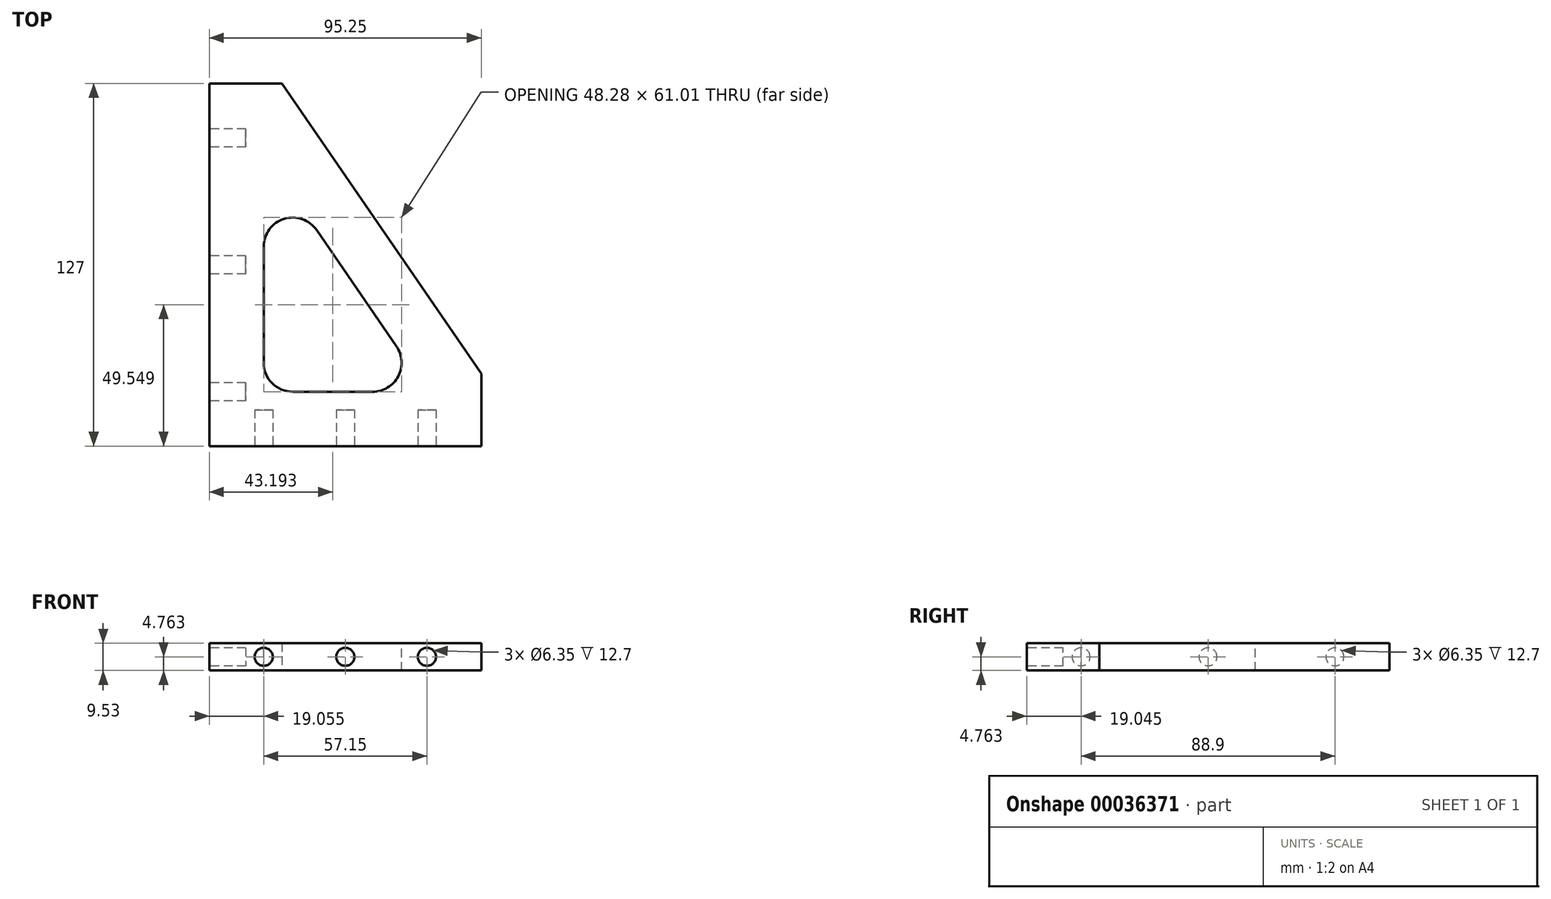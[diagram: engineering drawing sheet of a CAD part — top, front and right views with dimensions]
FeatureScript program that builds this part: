
annotation { "Feature Type Name" : "Feature", "Feature Type Description" : "" }
export const myFeature = defineFeature(function(context is Context, id is Id, definition is map)
    precondition{}
    {
        {
            var Q0;
            Q0=qCreatedBy(makeId("Top.planeOp"),FACE);
            var sketch = newSketch(context, id + "F0", { "sketchPlane" : qUnion([Q0])});
            skLineSegment(sketch, "E0", {"start": v(-41.93, 63.48) * mm, "end": v(-41.93, -63.52) * mm});
            skLineSegment(sketch, "E1", {"start": v(-41.93, 63.48) * mm, "end": v(-16.53, 63.48) * mm});
            skLineSegment(sketch, "E2", {"start": v(-41.93, -63.52) * mm, "end": v(53.32, -63.52) * mm});
            skLineSegment(sketch, "E3", {"start": v(53.32, -63.52) * mm, "end": v(53.32, -38.12) * mm});
            skLineSegment(sketch, "E4", {"start": v(-16.53, 63.48) * mm, "end": v(53.32, -38.12) * mm});
            skSolve(sketch);
        }
        {
            var Q0;
            Q0=makeQuery(id+"F0.imprint","IMPRINT",FACE,{"disambiguationData":[TD([[makeQuery(id+"F0.imprint","IMPRINT",EDGE,{"derivedFrom":sQuery(id+"F0.wireOp",EDGE,"E0")}),1.0]])]});
            var Q1;
            Q1 = qSketchRegion(id + "F0", true);
            extrude(context, id + "F1", {"entities" : qUnion([Q0, Q1]), "depth" : 9.52 * mm});
        }
        {
            var Q0;
            Q0=makeQuery(id+"F1.opExtrude","CAP_FACE",FACE,{"disambiguationData":[OSD([sQuery(id+"F0.wireOp",EDGE,"E0"),sQuery(id+"F0.wireOp",EDGE,"E1"),sQuery(id+"F0.wireOp",EDGE,"E2"),sQuery(id+"F0.wireOp",EDGE,"E3"),sQuery(id+"F0.wireOp",EDGE,"E4")])],"isStart":false});
            var sketch = newSketch(context, id + "F2", { "sketchPlane" : qUnion([Q0])});
            skLineSegment(sketch, "E5", {"start": v(-22.88, 6.37) * mm, "end": v(-22.88, -34.31) * mm});
            skLineSegment(sketch, "E6", {"start": v(-12.72, -44.47) * mm, "end": v(15.26, -44.47) * mm});
            skPoint(sketch, "E7.visualSharp", {"position": v(-22.88, -44.47) * mm});
            skArc(sketch, "E7.filletArc", {"start": v(-22.88, -34.31) * mm, "mid": v(-19.9, -41.5) * mm, "end": v(-12.72, -44.47) * mm});
            skLineSegment(sketch, "E8", {"start": v(-4.34, 12.13) * mm, "end": v(23.63, -28.56) * mm});
            skPoint(sketch, "E9.visualSharp", {"position": v(-22.88, 39.09) * mm});
            skArc(sketch, "E9.filletArc", {"start": v(-4.34, 12.13) * mm, "mid": v(-15.73, 16.08) * mm, "end": v(-22.88, 6.37) * mm});
            skPoint(sketch, "E10.visualSharp", {"position": v(34.57, -44.47) * mm});
            skArc(sketch, "E10.filletArc", {"start": v(15.26, -44.47) * mm, "mid": v(24.25, -39.04) * mm, "end": v(23.63, -28.56) * mm});
            skSolve(sketch);
        }
        {
            var Q0;
            Q0 = qSketchRegion(id + "F2", true);
            extrude(context, id + "F3", {"entities" : qUnion([Q0]), "operationType" : NewBodyOperationType.REMOVE, "endBound" : BoundingType.THROUGH_ALL, "oppositeDirection" : true, "depth" : 25.4 * mm});
        }
        {
            var Q0;
            Q0=makeQuery(id+"F1.opExtrude","SWEPT_FACE",FACE,{"disambiguationData":[OSD([sQuery(id+"F0.wireOp",EDGE,"E2")])]});
            var sketch = newSketch(context, id + "F4", { "sketchPlane" : qUnion([Q0])});
            skLineSegment(sketch, "E11", {"start": v(-41.93, 4.76) * mm, "end": v(53.32, 4.76) * mm});
            skLineSegment(sketch, "E12", {"start": v(53.32, 4.76) * mm, "end": v(-41.93, 4.76) * mm});
            skPoint(sketch, "E13", {"position": v(-22.88, 4.76) * mm});
            skPoint(sketch, "E14", {"position": v(5.7, 4.76) * mm});
            skPoint(sketch, "E15", {"position": v(34.27, 4.76) * mm});
            skCircle(sketch, "E16", {"center": v(-22.88, 4.76) * mm, "radius": 3.18 * mm});
            skCircle(sketch, "E17", {"center": v(5.7, 4.76) * mm, "radius": 3.18 * mm});
            skCircle(sketch, "E18", {"center": v(34.27, 4.76) * mm, "radius": 3.18 * mm});
            skSolve(sketch);
        }
        {
            var Q0;
            Q0=makeQuery(id+"F1.opExtrude","SWEPT_FACE",FACE,{"disambiguationData":[OSD([sQuery(id+"F0.wireOp",EDGE,"E0")])]});
            var sketch = newSketch(context, id + "F5", { "sketchPlane" : qUnion([Q0])});
            skLineSegment(sketch, "E19", {"start": v(-63.48, 4.76) * mm, "end": v(63.52, 4.76) * mm});
            skPoint(sketch, "E20", {"position": v(-44.43, 4.76) * mm});
            skPoint(sketch, "E21", {"position": v(0.02, 4.76) * mm});
            skPoint(sketch, "E22", {"position": v(44.47, 4.76) * mm});
            skCircle(sketch, "E23", {"center": v(-44.43, 4.76) * mm, "radius": 3.18 * mm});
            skCircle(sketch, "E24", {"center": v(0.02, 4.76) * mm, "radius": 3.18 * mm});
            skCircle(sketch, "E25", {"center": v(44.47, 4.76) * mm, "radius": 3.18 * mm});
            skSolve(sketch);
        }
        {
            var Q0;
            Q0 = qSketchRegion(id + "F5", true);
            extrude(context, id + "F6", {"entities" : qUnion([Q0]), "operationType" : NewBodyOperationType.REMOVE, "oppositeDirection" : true, "depth" : 12.7 * mm});
        }
        {
            var Q0;
            Q0 = qSketchRegion(id + "F4", true);
            extrude(context, id + "F7", {"entities" : qUnion([Q0]), "operationType" : NewBodyOperationType.REMOVE, "oppositeDirection" : true, "depth" : 12.7 * mm});
        }
        {
            var Q0;
            Q0 = qSketchRegion(id + "F4", true);
            extrude(context, id + "F8", {"entities" : qUnion([Q0]), "operationType" : NewBodyOperationType.REMOVE, "oppositeDirection" : true, "depth" : 12.7 * mm});
        }
    });
